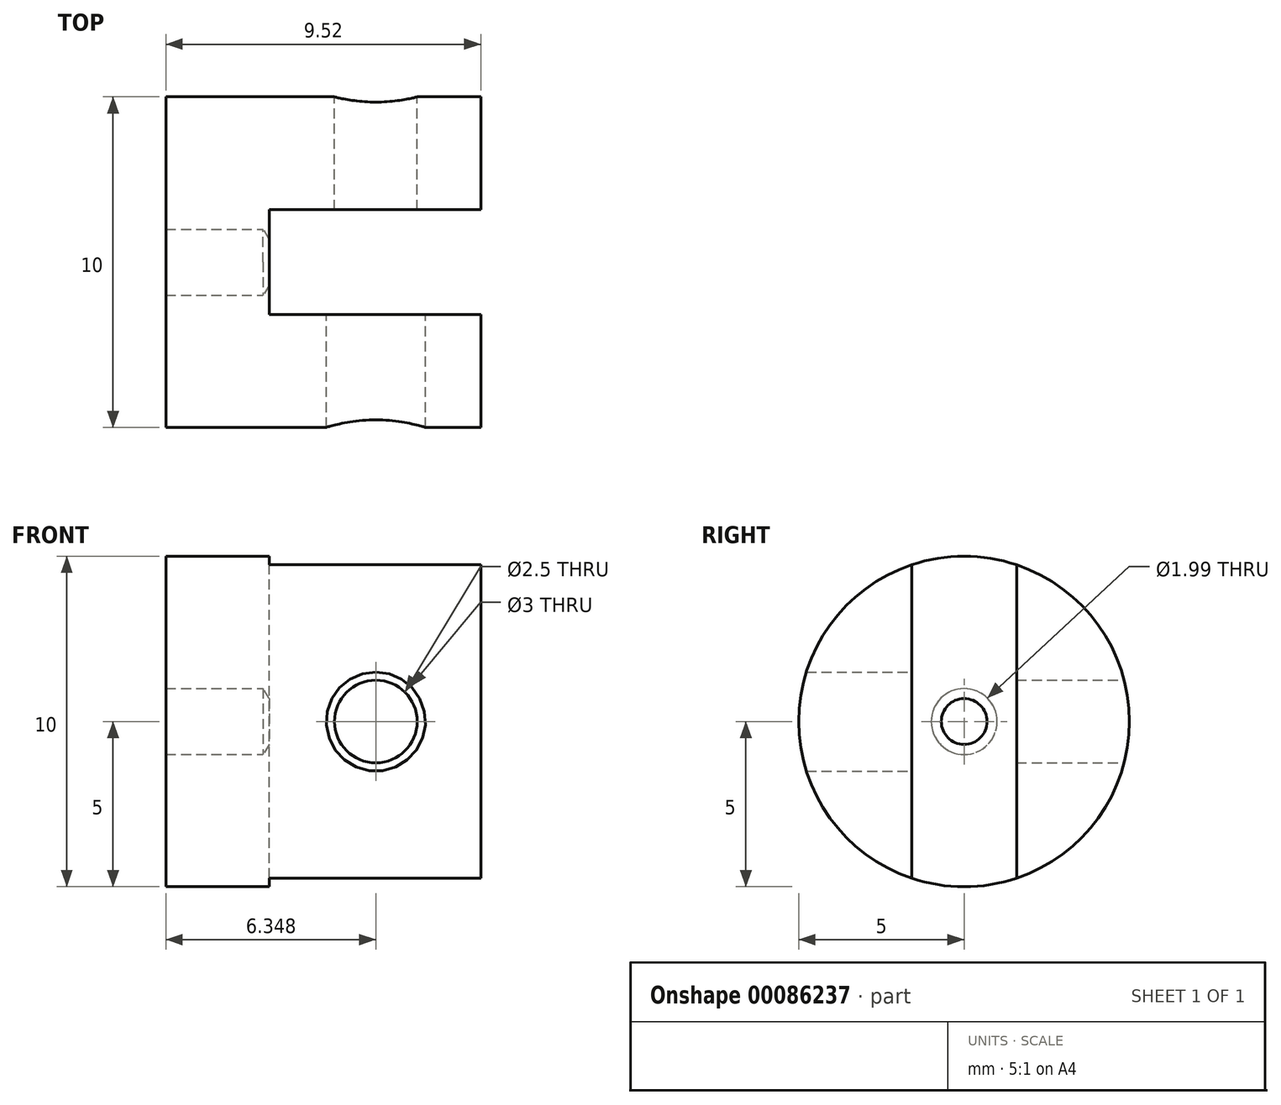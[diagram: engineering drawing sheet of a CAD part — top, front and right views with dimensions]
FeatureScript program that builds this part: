
annotation { "Feature Type Name" : "Feature", "Feature Type Description" : "" }
export const myFeature = defineFeature(function(context is Context, id is Id, definition is map)
    precondition{}
    {
        {
            var Q0;
            Q0=qCreatedBy(makeId("Right.planeOp"),FACE);
            var sketch = newSketch(context, id + "F0", { "sketchPlane" : qUnion([Q0])});
            skCircle(sketch, "E0", {"center": v(0, 0) * mm, "radius": 5 * mm});
            skSolve(sketch);
        }
        {
            var Q0;
            Q0=makeQuery(id+"F0.imprint","IMPRINT",FACE,{"disambiguationData":[TD([[makeQuery(id+"F0.imprint","IMPRINT",EDGE,{"derivedFrom":sQuery(id+"F0.wireOp",EDGE,"E0")}),1.0]])]});
            extrude(context, id + "F1", {"entities" : qUnion([Q0]), "depth" : 25.4 * .375 * mm, "symmetric" : true});
        }
        {
            var Q0;
            Q0=makeQuery(id+"F1.opExtrude","CAP_FACE",FACE,{"disambiguationData":[OSD([sQuery(id+"F0.wireOp",EDGE,"E0")])],"isStart":true});
            var sketch = newSketch(context, id + "F2", { "sketchPlane" : qUnion([Q0])});
            skPoint(sketch, "E1", {"position": v(0, 0) * mm});
            skSolve(sketch);
        }
        {
            var Q0;
            Q0=sQuery(id+"F2.wireOp",VERTEX,"E1");
            var Q1;
            Q1=makeQuery(id+"F1.opExtrude","SWEPT_BODY",BODY,{"disambiguationData":[OSD([sQuery(id+"F0.wireOp",EDGE,"E0")])]});
            hole(context, id + "F3", {"style" : HoleStyle.SIMPLE, "endStyle" : HoleEndStyle.BLIND, "standardTappedOrClearance" : lookupTablePath({ "standard" : "ANSI", "engagement" : "75%", "pitch" : "48 tpi", "size" : "#3", "type" : "Tapped" }), "standardBlindInLast" : lookupTablePath({ "standard" : "ANSI", "engagement" : "75%", "pitch" : "48 tpi", "size" : "#3", "type" : "Tapped" }), "holeDiameter" : 2 * mm, "showTappedDepth" : true, "holeDepth" : 2.94 * mm, "tappedDepth" : 2.41 * mm, "tapClearance" : 1, "locations" : qUnion([Q0]), "scope" : qUnion([Q1]), "majorDiameter" : 2.5 * mm});
        }
        {
            var Q0;
            Q0=qCreatedBy(makeId("Top.planeOp"),FACE);
            var sketch = newSketch(context, id + "F4", { "sketchPlane" : qUnion([Q0])});
            skLineSegment(sketch, "E2.bottom", {"start": v(-1.64, 1.59) * mm, "end": v(11.16, 1.59) * mm});
            skLineSegment(sketch, "E2.top", {"start": v(-1.64, -1.59) * mm, "end": v(11.16, -1.59) * mm});
            skLineSegment(sketch, "E2.left", {"start": v(-1.64, 1.59) * mm, "end": v(-1.64, -1.59) * mm});
            skLineSegment(sketch, "E2.right", {"start": v(11.16, 1.59) * mm, "end": v(11.16, -1.59) * mm});
            skPoint(sketch, "E2.middle", {"position": v(4.76, 0) * mm});
            skSolve(sketch);
        }
        {
            var Q0;
            Q0=makeQuery(id+"F4.imprint","IMPRINT",FACE,{"disambiguationData":[TD([[makeQuery(id+"F4.imprint","IMPRINT",EDGE,{"derivedFrom":sQuery(id+"F4.wireOp",EDGE,"E2.bottom")}),-1.0]])]});
            extrude(context, id + "F5", {"entities" : qUnion([Q0]), "operationType" : NewBodyOperationType.REMOVE, "oppositeDirection" : true, "depth" : 25 * mm, "symmetric" : true});
        }
        {
            var Q0;
            Q0=makeQuery(id+"F5.boolean.opBoolean","COPY",FACE,{"derivedFrom":makeQuery(id+"F5.opExtrude","SWEPT_FACE",FACE,{"disambiguationData":[OSD([sQuery(id+"F4.wireOp",EDGE,"E2.bottom")])]})});
            var sketch = newSketch(context, id + "F6", { "sketchPlane" : qUnion([Q0])});
            skPoint(sketch, "E3", {"position": v(1.59, 0) * mm});
            skSolve(sketch);
        }
        {
            var Q0;
            Q0=sQuery(id+"F6.wireOp",VERTEX,"E3");
            var Q1;
            Q1=makeQuery(id+"F1.opExtrude","SWEPT_BODY",BODY,{"disambiguationData":[OSD([sQuery(id+"F0.wireOp",EDGE,"E0")])]});
            hole(context, id + "F7", {"style" : HoleStyle.SIMPLE, "endStyle" : HoleEndStyle.THROUGH, "standardTappedOrClearance" : lookupTablePath({ "standard" : "ISO", "engagement" : "75%", "pitch" : "0.5 mm", "size" : "M3", "type" : "Tapped" }), "standardBlindInLast" : lookupTablePath({ "standard" : "ISO", "engagement" : "75%", "pitch" : "0.5 mm", "size" : "M3", "type" : "Tapped" }), "holeDiameter" : 2.5 * mm, "showTappedDepth" : true, "isTappedThrough" : true, "tappedDepth" : 3.47 * mm, "tapClearance" : 1, "locations" : qUnion([Q0]), "scope" : qUnion([Q1]), "majorDiameter" : 3 * mm});
        }
        {
            var Q0;
            Q0=makeQuery(id+"F5.boolean.opBoolean","COPY",FACE,{"derivedFrom":makeQuery(id+"F5.opExtrude","SWEPT_FACE",FACE,{"disambiguationData":[OSD([sQuery(id+"F4.wireOp",EDGE,"E2.top")])]})});
            var sketch = newSketch(context, id + "F8", { "sketchPlane" : qUnion([Q0])});
            skCircle(sketch, "E4.0", {"center": v(-1.59, 0) * mm, "radius": 1.25 * mm, "construction": true});
            skCircle(sketch, "E5", {"center": v(-1.59, 0) * mm, "radius": 1.5 * mm});
            skSolve(sketch);
        }
        {
            var Q0;
            Q0 = qSketchRegion(id + "F8", true);
            extrude(context, id + "F9", {"entities" : qUnion([Q0]), "operationType" : NewBodyOperationType.REMOVE, "endBound" : BoundingType.THROUGH_ALL, "oppositeDirection" : true, "depth" : 25 * mm});
        }
    });
